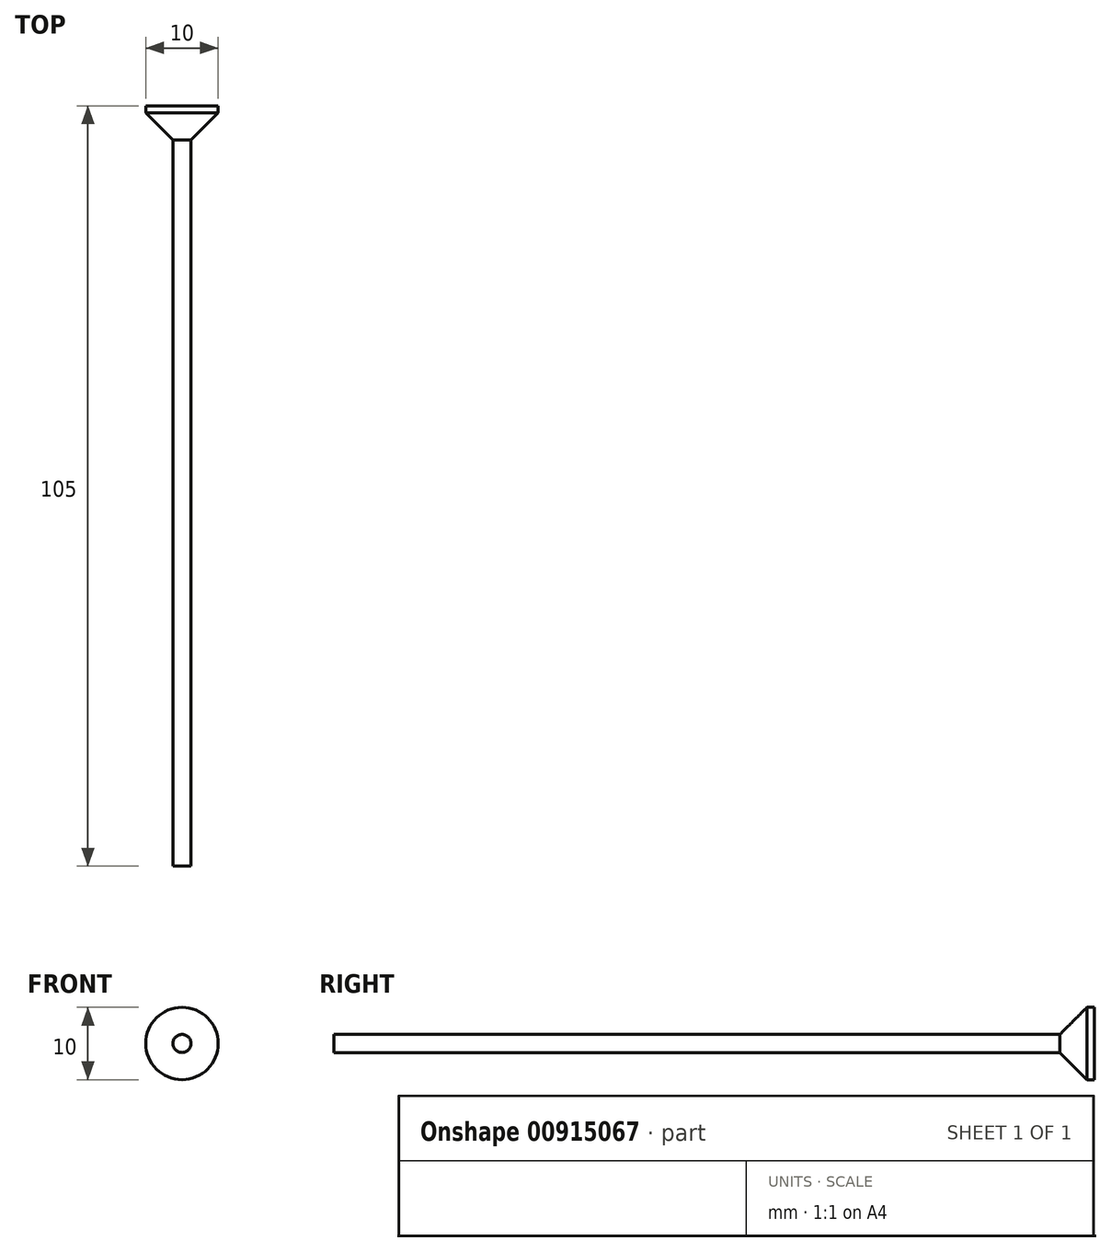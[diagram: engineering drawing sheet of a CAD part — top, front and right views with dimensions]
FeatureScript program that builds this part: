
annotation { "Feature Type Name" : "Feature", "Feature Type Description" : "" }
export const myFeature = defineFeature(function(context is Context, id is Id, definition is map)
    precondition{}
    {
        {
            var Q0;
            Q0=qCreatedBy(makeId("Front.planeOp"),FACE);
            var sketch = newSketch(context, id + "F0", { "sketchPlane" : qUnion([Q0])});
            skCircle(sketch, "E0", {"center": v(0, 0) * mm, "radius": 5 * mm});
            skSolve(sketch);
        }
        {
            var Q0;
            Q0 = qSketchRegion(id + "F0", true);
            extrude(context, id + "F1", {"entities" : qUnion([Q0]), "depth" : 5 * mm, "offsetDistance" : 25 * mm});
        }
        {
            var Q0;
            Q0=makeQuery(id+"F1.opExtrude","CAP_FACE",FACE,{"disambiguationData":[OSD([sQuery(id+"F0.wireOp",EDGE,"E0")])],"isStart":false});
            var sketch = newSketch(context, id + "F2", { "sketchPlane" : qUnion([Q0])});
            skCircle(sketch, "E1", {"center": v(0, 0) * mm, "radius": 1.25 * mm});
            skSolve(sketch);
        }
        {
            var Q0;
            Q0 = qSketchRegion(id + "F2", true);
            extrude(context, id + "F3", {"entities" : qUnion([Q0]), "operationType" : NewBodyOperationType.ADD, "depth" : 100 * mm, "offsetDistance" : 25 * mm});
        }
        {
            var Q0;
            Q0=makeQuery(id+"F1.opExtrude","CAP_EDGE",EDGE,{"disambiguationData":[OSD([sQuery(id+"F0.wireOp",EDGE,"E0")])],"isStart":false});
            chamfer(context, id + "F4", {"entities" : qUnion([Q0]), "width" : 4 * mm, "tangentPropagation" : true});
        }
    });
